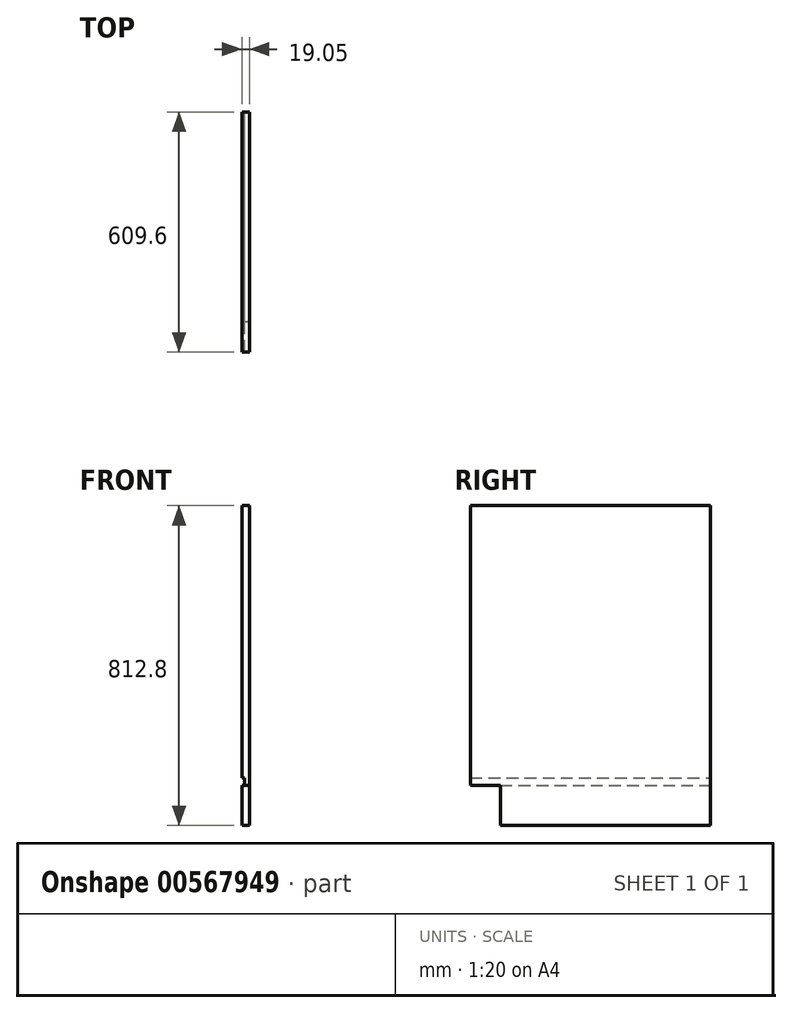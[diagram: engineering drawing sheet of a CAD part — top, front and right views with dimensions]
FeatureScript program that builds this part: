
annotation { "Feature Type Name" : "Feature", "Feature Type Description" : "" }
export const myFeature = defineFeature(function(context is Context, id is Id, definition is map)
    precondition{}
    {
        {
            var Q0;
            Q0=qCreatedBy(makeId("Right.planeOp"),FACE);
            var sketch = newSketch(context, id + "F0", { "sketchPlane" : qUnion([Q0])});
            skLineSegment(sketch, "E0", {"start": v(0, 0) * mm, "end": v(0, 101.6) * mm});
            skLineSegment(sketch, "E1", {"start": v(0, 101.6) * mm, "end": v(-76.2, 101.6) * mm});
            skLineSegment(sketch, "E2", {"start": v(-76.2, 101.6) * mm, "end": v(-76.2, 812.8) * mm});
            skLineSegment(sketch, "E3", {"start": v(-76.2, 812.8) * mm, "end": v(533.4, 812.8) * mm});
            skLineSegment(sketch, "E4", {"start": v(533.4, 812.8) * mm, "end": v(533.4, 0) * mm});
            skLineSegment(sketch, "E5", {"start": v(533.4, 0) * mm, "end": v(0, 0) * mm});
            skSolve(sketch);
        }
        {
            var Q0;
            Q0 = qSketchRegion(id + "F0", true);
            extrude(context, id + "F1", {"entities" : qUnion([Q0]), "depth" : 19.05 * mm, "offsetDistance" : 25.4 * mm});
        }
        {
            var Q0;
            Q0=makeQuery(id+"F1.opExtrude","CAP_FACE",FACE,{"disambiguationData":[OSD([sQuery(id+"F0.wireOp",EDGE,"E0"),sQuery(id+"F0.wireOp",EDGE,"E1"),sQuery(id+"F0.wireOp",EDGE,"E2"),sQuery(id+"F0.wireOp",EDGE,"E3"),sQuery(id+"F0.wireOp",EDGE,"E4"),sQuery(id+"F0.wireOp",EDGE,"E5")])],"isStart":true});
            var sketch = newSketch(context, id + "F2", { "sketchPlane" : qUnion([Q0])});
            skLineSegment(sketch, "E6.bottom", {"start": v(76.2, 101.6) * mm, "end": v(-533.4, 101.6) * mm});
            skLineSegment(sketch, "E6.top", {"start": v(76.2, 120.65) * mm, "end": v(-533.4, 120.65) * mm});
            skLineSegment(sketch, "E6.left", {"start": v(76.2, 101.6) * mm, "end": v(76.2, 120.65) * mm});
            skLineSegment(sketch, "E6.right", {"start": v(-533.4, 101.6) * mm, "end": v(-533.4, 120.65) * mm});
            skSolve(sketch);
        }
        {
            var Q0;
            Q0=makeQuery(id+"F2.imprint","IMPRINT",FACE,{"disambiguationData":[TD([[makeQuery(id+"F2.imprint","IMPRINT",EDGE,{"derivedFrom":sQuery(id+"F2.wireOp",EDGE,"E6.top")}),1.0]])]});
            extrude(context, id + "F3", {"entities" : qUnion([Q0]), "operationType" : NewBodyOperationType.REMOVE, "oppositeDirection" : true, "depth" : 6.35 * mm, "offsetDistance" : 25.4 * mm});
        }
    });
